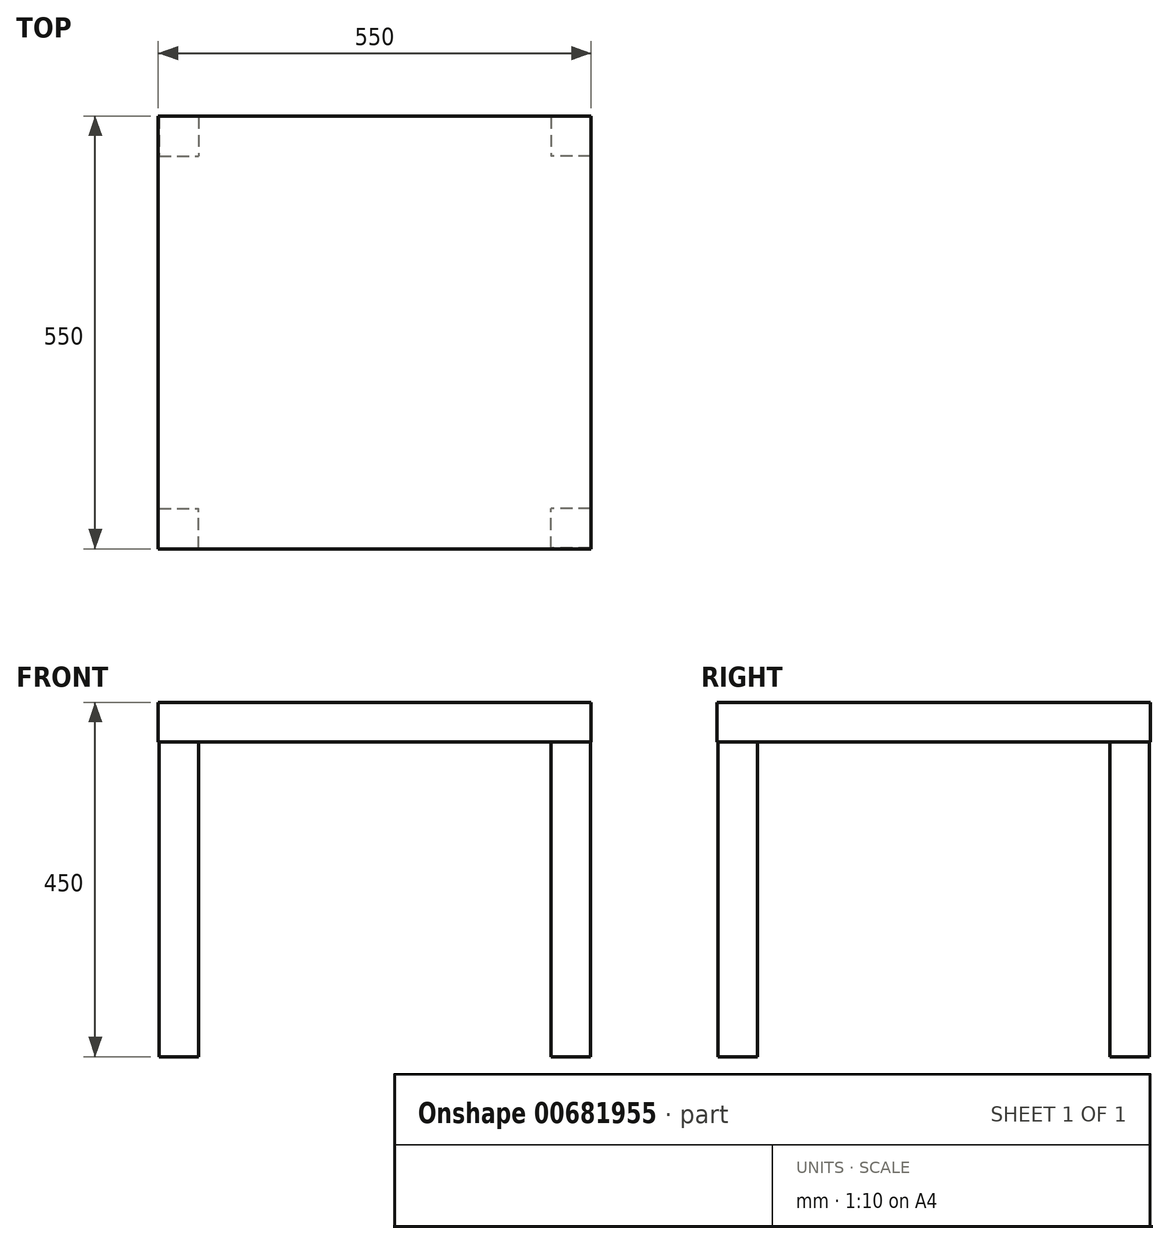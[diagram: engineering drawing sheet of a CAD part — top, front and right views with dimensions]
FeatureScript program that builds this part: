
annotation { "Feature Type Name" : "Feature", "Feature Type Description" : "" }
export const myFeature = defineFeature(function(context is Context, id is Id, definition is map)
    precondition{}
    {
        {
            var Q0;
            Q0=qCreatedBy(makeId("Top.planeOp"),FACE);
            var sketch = newSketch(context, id + "F0", { "sketchPlane" : qUnion([Q0])});
            skLineSegment(sketch, "E0.bottom", {"start": v(-275, 275) * mm, "end": v(275, 275) * mm});
            skLineSegment(sketch, "E0.top", {"start": v(-275, -275) * mm, "end": v(275, -275) * mm});
            skLineSegment(sketch, "E0.left", {"start": v(-275, 275) * mm, "end": v(-275, -275) * mm});
            skLineSegment(sketch, "E0.right", {"start": v(275, 275) * mm, "end": v(275, -275) * mm});
            skPoint(sketch, "E0.middle", {"position": v(0, 0) * mm});
            skLineSegment(sketch, "E1.bottom", {"start": v(-273.94, 273.94) * mm, "end": v(-223.94, 273.94) * mm});
            skLineSegment(sketch, "E1.top", {"start": v(-273.94, 223.94) * mm, "end": v(-223.94, 223.94) * mm});
            skLineSegment(sketch, "E1.left", {"start": v(-273.94, 273.94) * mm, "end": v(-273.94, 223.94) * mm});
            skLineSegment(sketch, "E1.right", {"start": v(-223.94, 273.94) * mm, "end": v(-223.94, 223.94) * mm});
            skLineSegment(sketch, "E2.bottom", {"start": v(273.94, 273.94) * mm, "end": v(223.94, 273.94) * mm});
            skLineSegment(sketch, "E2.top", {"start": v(273.94, 223.94) * mm, "end": v(223.94, 223.94) * mm});
            skLineSegment(sketch, "E2.left", {"start": v(273.94, 273.94) * mm, "end": v(273.94, 223.94) * mm});
            skLineSegment(sketch, "E2.right", {"start": v(223.94, 273.94) * mm, "end": v(223.94, 223.94) * mm});
            skLineSegment(sketch, "E3.bottom", {"start": v(273.94, -273.94) * mm, "end": v(223.94, -273.94) * mm});
            skLineSegment(sketch, "E3.top", {"start": v(273.94, -223.94) * mm, "end": v(223.94, -223.94) * mm});
            skLineSegment(sketch, "E3.left", {"start": v(273.94, -273.94) * mm, "end": v(273.94, -223.94) * mm});
            skLineSegment(sketch, "E3.right", {"start": v(223.94, -273.94) * mm, "end": v(223.94, -223.94) * mm});
            skLineSegment(sketch, "E4.bottom", {"start": v(-273.94, -273.94) * mm, "end": v(-223.94, -273.94) * mm});
            skLineSegment(sketch, "E4.top", {"start": v(-273.94, -223.94) * mm, "end": v(-223.94, -223.94) * mm});
            skLineSegment(sketch, "E4.left", {"start": v(-273.94, -273.94) * mm, "end": v(-273.94, -223.94) * mm});
            skLineSegment(sketch, "E4.right", {"start": v(-223.94, -273.94) * mm, "end": v(-223.94, -223.94) * mm});
            skLineSegment(sketch, "E5", {"start": v(-275, 275) * mm, "end": v(-273.94, 273.94) * mm});
            skSolve(sketch);
        }
        {
            var Q0;
            Q0 = qSketchRegion(id + "F0", true);
            var Q1;
            Q1=makeQuery(id+"F0.imprint","IMPRINT",FACE,{"disambiguationData":[TD([[makeQuery(id+"F0.imprint","IMPRINT",EDGE,{"derivedFrom":sQuery(id+"F0.wireOp",EDGE,"E1.bottom")}),-1.0]])]});
            var Q2;
            Q2=makeQuery(id+"F0.imprint","IMPRINT",FACE,{"disambiguationData":[TD([[makeQuery(id+"F0.imprint","IMPRINT",EDGE,{"derivedFrom":sQuery(id+"F0.wireOp",EDGE,"E4.bottom")}),1.0]])]});
            var Q3;
            Q3=makeQuery(id+"F0.imprint","IMPRINT",FACE,{"disambiguationData":[TD([[makeQuery(id+"F0.imprint","IMPRINT",EDGE,{"derivedFrom":sQuery(id+"F0.wireOp",EDGE,"E3.bottom")}),-1.0]])]});
            var Q4;
            Q4=makeQuery(id+"F0.imprint","IMPRINT",FACE,{"disambiguationData":[TD([[makeQuery(id+"F0.imprint","IMPRINT",EDGE,{"derivedFrom":sQuery(id+"F0.wireOp",EDGE,"E2.bottom")}),1.0]])]});
            extrude(context, id + "F1", {"entities" : qUnion([Q0, Q1, Q2, Q3, Q4]), "depth" : 50 * mm, "offsetDistance" : 25 * mm});
        }
        {
            var Q0;
            Q0=makeQuery(id+"F0.imprint","IMPRINT",FACE,{"disambiguationData":[TD([[makeQuery(id+"F0.imprint","IMPRINT",EDGE,{"derivedFrom":sQuery(id+"F0.wireOp",EDGE,"E4.bottom")}),1.0]])]});
            var Q1;
            Q1=makeQuery(id+"F0.imprint","IMPRINT",FACE,{"disambiguationData":[TD([[makeQuery(id+"F0.imprint","IMPRINT",EDGE,{"derivedFrom":sQuery(id+"F0.wireOp",EDGE,"E3.bottom")}),-1.0]])]});
            var Q2;
            Q2=makeQuery(id+"F0.imprint","IMPRINT",FACE,{"disambiguationData":[TD([[makeQuery(id+"F0.imprint","IMPRINT",EDGE,{"derivedFrom":sQuery(id+"F0.wireOp",EDGE,"E2.bottom")}),1.0]])]});
            var Q3;
            Q3=makeQuery(id+"F0.imprint","IMPRINT",FACE,{"disambiguationData":[TD([[makeQuery(id+"F0.imprint","IMPRINT",EDGE,{"derivedFrom":sQuery(id+"F0.wireOp",EDGE,"E1.bottom")}),-1.0]])]});
            extrude(context, id + "F2", {"entities" : qUnion([Q0, Q1, Q2, Q3]), "operationType" : NewBodyOperationType.ADD, "oppositeDirection" : true, "depth" : 400 * mm, "offsetDistance" : 25 * mm});
        }
    });
